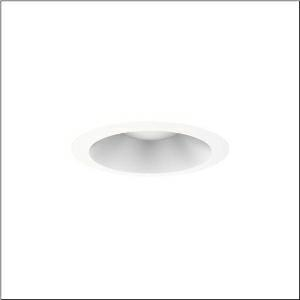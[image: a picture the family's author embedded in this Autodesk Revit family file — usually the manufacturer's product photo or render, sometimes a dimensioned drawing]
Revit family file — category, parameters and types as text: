
# Revit family: lunis_31-xl_51dn15mg32b
name_source: partatom
category: Lighting Fixtures
units: mm (PartAtom-declared; Revit-internal decimal feet)

## family parameters
Cut with Voids When Loaded = No
Host = Face
Light Source = No
Part Type = Normal
Room Calculation Point = No
Round Connector Dimension = Use Diameter
Shared = No

## types (1)
- --- (1 x LED, 2400 lm, 17 W, 3000K)
    Apparent Load = 17 VA
    CIE Flux Codes = 89 99 100 100 100
    Color Rendering = 80
    Color Temperature = 3000K
    Default Elevation = 1800 mm
    Description = Lunis 31, -XL, downlight, light control with lens, light emission: direct distribution, LED rated luminous flux: 2.400lm, light colour: 830, mains connection: 220..240V, AC, 50/60Hz, housing, of aluminium, white, protection rating (complete): IP20, protection rating (on room side): IP54, insulation class (complete): insulation class II (safety insulation), certification: CE, packaging unit: 1 piece
    Height = 0 mm  [stored 0 ft]
    Lamp = 1 x LED
    Lamp Light Flux = 2400 lm
    Lamp Power = 17 W
    Lamp count = 1
    Length = 259 mm
    Luminous efficacy = 141 lm/W
    Manufacturer = Siteco
    ModVariant = No
    Model = 51DN15MG32B
    Mounting Place = Ceiling
    Mounting Type = Recessed
    Number of Poles = 1
    OnlyDefault = Yes
    Power Factor = 1
    Product Name = Lunis 31-XL
    Product group = downlight
    ProductGroupID = 400
    Protection Class = Protection class II
    Protection Degree = IP 20
    RLX_Detail_Level = 1
    RLX_Emergency_Light_Flux = 0 lm
    RLX_Emergency_Type = 0
    RLX_Emergency_Type_DB = No
    RlxData = <blob elided: 24301 chars, md5=a3edfa0a>
    Socket = socket
    Standby Power = 0 W
    System Light Flux = 2400 lm
    System Power = 17 W
    Type Comments = individual setting: luminous flux: 100 % | (ON | ON | ON | OFF) | 450 mA
    Type Image = l_1345915.jpg
    URL = http://relux.com
    VarID = @adj_010089
    Voltage = 0 V
    Weight = 0.00 kg
    Width = 0 mm  [stored 0 ft]

note: [stored X ft] marks values corroborated as IEEE doubles in the binary element streams (Revit-internal decimal feet)

## geometry (parser evidence)
native form markers: Blend x4, Sweep x11
no freeform markers — native parametric forms only
